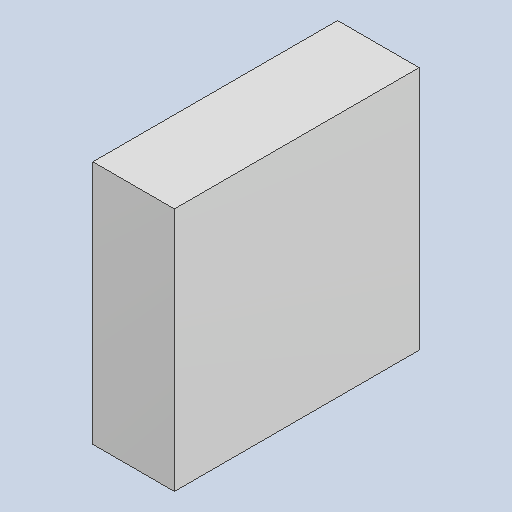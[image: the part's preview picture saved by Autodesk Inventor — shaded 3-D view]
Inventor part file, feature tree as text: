
AUTODESK INVENTOR PART (.ipt)
format: ipt  version: 2023.4 (Build 274418000, 418)  size: 81,408 bytes
history: native  units: mm
features: extrude x1
ambient origin geometry x8: Origin, YZ Plane, XZ Plane, XY Plane, X Axis, Y Axis, Z Axis, Center Point
bodies: Solid1 (feature_tree)
feature tree (1):
  extrude  "Extruded_34"  [1 undecoded]
note: 1 required parameter value undecoded (feature->parameter linkage not recoverable at this tier; creation-order binding heuristic only, values carry confidence <= 0.55)
